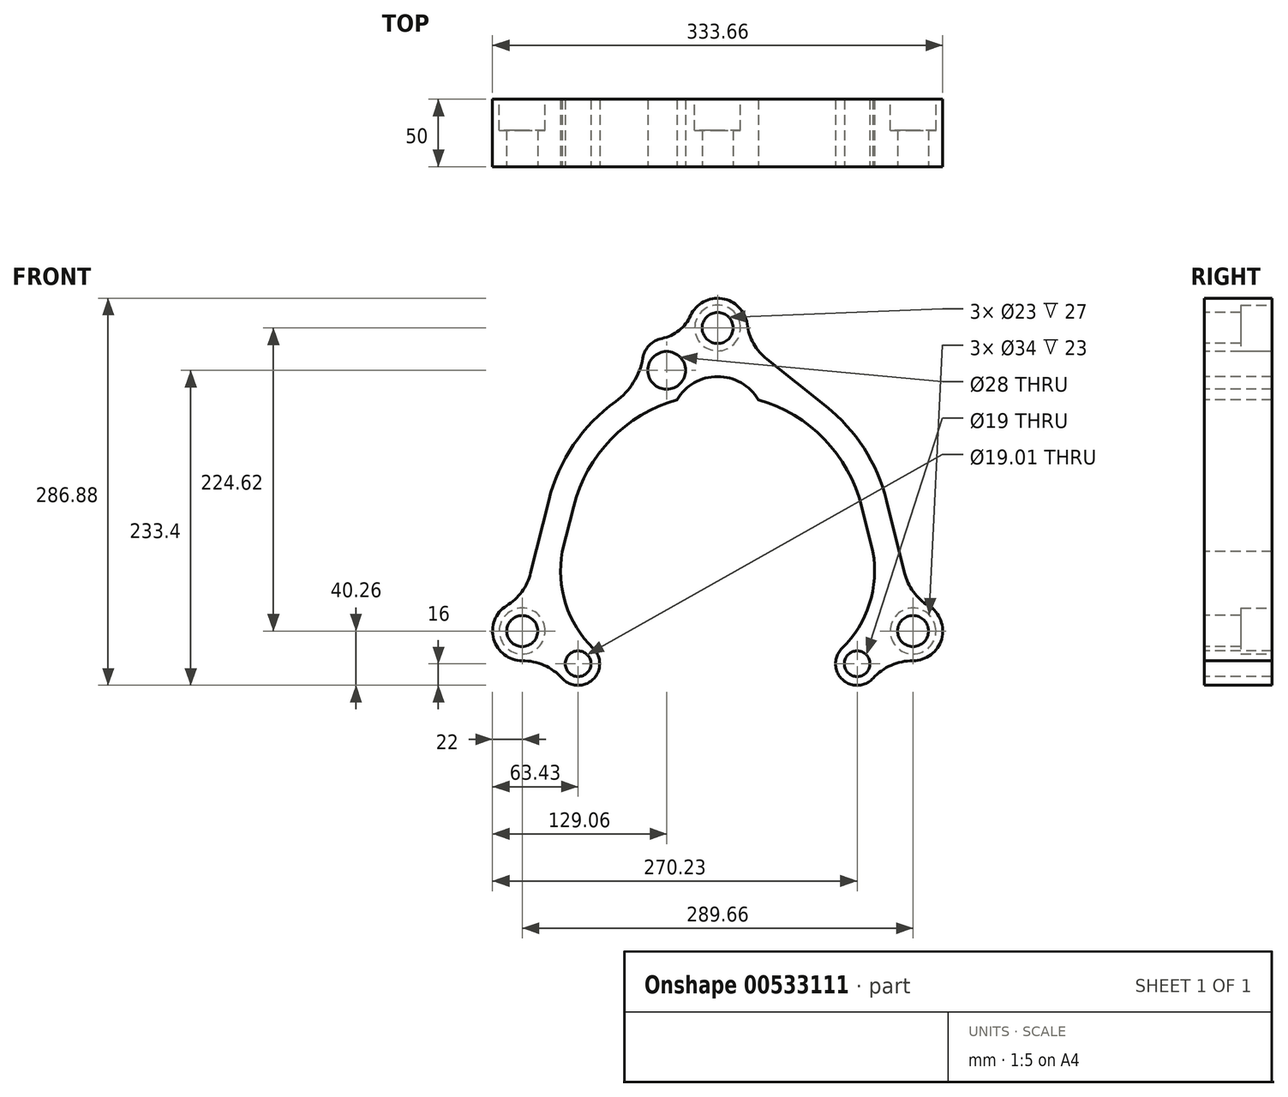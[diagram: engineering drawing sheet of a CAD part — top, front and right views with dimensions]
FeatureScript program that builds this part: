
annotation { "Feature Type Name" : "Feature", "Feature Type Description" : "" }
export const myFeature = defineFeature(function(context is Context, id is Id, definition is map)
    precondition{}
    {
        {
            var Q0;
            Q0=qCreatedBy(makeId("Front.planeOp"),FACE);
            var sketch = newSketch(context, id + "F0", { "sketchPlane" : qUnion([Q0])});
            skArc(sketch, "E0", {"start": v(-30.14, 105.79) * mm, "mid": v(-79.06, 76.48) * mm, "end": v(-106.73, 26.61) * mm});
            skArc(sketch, "E1", {"start": v(30.14, 105.79) * mm, "mid": v(0, 123) * mm, "end": v(-30.14, 105.79) * mm});
            skPoint(sketch, "E2.endSnap0", {"position": v(0, -110) * mm});
            skArc(sketch, "E3", {"start": v(144.8, -87.62) * mm, "mid": v(166, -71.63) * mm, "end": v(156.38, -46.9) * mm});
            skArc(sketch, "E4", {"start": v(125.17, 31.2) * mm, "mid": v(108.5, 69.79) * mm, "end": v(80.3, 100.96) * mm});
            skLineSegment(sketch, "E5", {"start": v(125.17, 31.2) * mm, "end": v(138.57, -22.53) * mm});
            skArc(sketch, "E6", {"start": v(138.57, -22.53) * mm, "mid": v(145.09, -36.46) * mm, "end": v(156.38, -46.9) * mm});
            skLineSegment(sketch, "E7", {"start": v(36.58, 135.74) * mm, "end": v(80.3, 100.96) * mm});
            skArc(sketch, "E8", {"start": v(21.81, 161.85) * mm, "mid": v(3.28, 180.75) * mm, "end": v(-20, 168.15) * mm});
            skArc(sketch, "E9", {"start": v(21.81, 161.85) * mm, "mid": v(26.65, 147.36) * mm, "end": v(36.58, 135.74) * mm});
            skArc(sketch, "E10", {"start": v(-41.34, 151.23) * mm, "mid": v(-50.68, 146.13) * mm, "end": v(-55.5, 136.64) * mm});
            skArc(sketch, "E11", {"start": v(-41.34, 151.23) * mm, "mid": v(-28.64, 157.13) * mm, "end": v(-20, 168.15) * mm});
            skArc(sketch, "E12", {"start": v(-75.52, 104.59) * mm, "mid": v(-62.37, 118.65) * mm, "end": v(-55.5, 136.64) * mm});
            skArc(sketch, "E13.trimOffspring", {"start": v(-75.52, 104.59) * mm, "mid": v(-106.84, 72.3) * mm, "end": v(-125.17, 31.2) * mm});
            skPoint(sketch, "E14.trimOffspring.center.orphan", {"position": v(5.86, 0) * mm});
            skArc(sketch, "E15.trimOffspring", {"start": v(106.73, 26.61) * mm, "mid": v(79.06, 76.48) * mm, "end": v(30.14, 105.79) * mm});
            skArc(sketch, "E16", {"start": v(92.23, -78.43) * mm, "mid": v(92.28, -101.38) * mm, "end": v(115.22, -100.66) * mm});
            skArc(sketch, "E17", {"start": v(144.8, -87.62) * mm, "mid": v(128.64, -91.02) * mm, "end": v(115.22, -100.66) * mm});
            skArc(sketch, "E18", {"start": v(92.23, -78.43) * mm, "mid": v(112.58, -45.47) * mm, "end": v(115.07, -6.82) * mm});
            skLineSegment(sketch, "E19", {"start": v(106.73, 26.61) * mm, "end": v(115.07, -6.82) * mm});
            skLineSegment(sketch, "E20", {"start": v(0, 88) * mm, "end": v(0, -110) * mm});
            skLineSegment(sketch, "E21.MirrorCS", {"start": v(-106.73, 26.61) * mm, "end": v(-115.07, -6.82) * mm});
            skLineSegment(sketch, "E22.MirrorCS", {"start": v(-125.17, 31.2) * mm, "end": v(-138.57, -22.53) * mm});
            skArc(sketch, "E23.MirrorCS", {"start": v(-138.57, -22.53) * mm, "mid": v(-145.09, -36.46) * mm, "end": v(-156.38, -46.9) * mm});
            skArc(sketch, "E24.MirrorCS", {"start": v(-144.8, -87.62) * mm, "mid": v(-166, -71.63) * mm, "end": v(-156.38, -46.9) * mm});
            skArc(sketch, "E25.MirrorCS", {"start": v(-144.8, -87.62) * mm, "mid": v(-128.64, -91.02) * mm, "end": v(-115.22, -100.66) * mm});
            skArc(sketch, "E26.MirrorCS", {"start": v(-92.23, -78.43) * mm, "mid": v(-92.28, -101.38) * mm, "end": v(-115.22, -100.66) * mm});
            skArc(sketch, "E27.MirrorCS", {"start": v(-92.23, -78.43) * mm, "mid": v(-112.58, -45.47) * mm, "end": v(-115.07, -6.82) * mm});
            skSolve(sketch);
        }
        {
            var Q0;
            Q0 = qSketchRegion(id + "F0", true);
            extrude(context, id + "F1", {"entities" : qUnion([Q0]), "oppositeDirection" : true, "depth" : 50 * mm, "offsetDistance" : 25 * mm});
        }
        {
            var Q0;
            Q0=qCreatedBy(makeId("Front.planeOp"),FACE);
            var sketch = newSketch(context, id + "F2", { "sketchPlane" : qUnion([Q0])});
            skCircle(sketch, "E28", {"center": v(0, 159) * mm, "radius": 11.5 * mm});
            skCircle(sketch, "E29", {"center": v(144.83, -65.62) * mm, "radius": 11.5 * mm});
            skCircle(sketch, "E30", {"center": v(-144.83, -65.62) * mm, "radius": 11.5 * mm});
            skSolve(sketch);
        }
        {
            var Q0;
            Q0 = qSketchRegion(id + "F2", true);
            extrude(context, id + "F3", {"entities" : qUnion([Q0]), "operationType" : NewBodyOperationType.REMOVE, "oppositeDirection" : true, "depth" : 64 * mm, "offsetDistance" : 25 * mm});
        }
        {
            var Q0;
            Q0=qCreatedBy(makeId("Front.planeOp"),FACE);
            var sketch = newSketch(context, id + "F4", { "sketchPlane" : qUnion([Q0])});
            skCircle(sketch, "E31", {"center": v(-37.77, 127.52) * mm, "radius": 14 * mm});
            skSolve(sketch);
        }
        {
            var Q0;
            Q0 = qSketchRegion(id + "F4", true);
            extrude(context, id + "F5", {"entities" : qUnion([Q0]), "operationType" : NewBodyOperationType.REMOVE, "oppositeDirection" : true, "depth" : 62 * mm, "offsetDistance" : 25 * mm});
        }
        {
            var Q0;
            Q0=qCreatedBy(makeId("Front.planeOp"),FACE);
            var sketch = newSketch(context, id + "F6", { "sketchPlane" : qUnion([Q0])});
            skCircle(sketch, "E32", {"center": v(-103.4, -89.88) * mm, "radius": 9.5 * mm});
            skCircle(sketch, "E33", {"center": v(103.4, -89.88) * mm, "radius": 9.5 * mm});
            skSolve(sketch);
        }
        {
            var Q0;
            Q0 = qSketchRegion(id + "F6", true);
            extrude(context, id + "F7", {"entities" : qUnion([Q0]), "operationType" : NewBodyOperationType.REMOVE, "oppositeDirection" : true, "depth" : 58 * mm, "offsetDistance" : 25 * mm});
        }
        {
            var Q0;
            Q0=makeQuery(id+"F1.opExtrude","CAP_FACE",FACE,{"disambiguationData":[OSD([sQuery(id+"F0.wireOp",EDGE,"E0"),sQuery(id+"F0.wireOp",EDGE,"E1"),sQuery(id+"F0.wireOp",EDGE,"E3"),sQuery(id+"F0.wireOp",EDGE,"E4"),sQuery(id+"F0.wireOp",EDGE,"E5"),sQuery(id+"F0.wireOp",EDGE,"E6"),sQuery(id+"F0.wireOp",EDGE,"E7"),sQuery(id+"F0.wireOp",EDGE,"E8"),sQuery(id+"F0.wireOp",EDGE,"E9"),sQuery(id+"F0.wireOp",EDGE,"E10"),sQuery(id+"F0.wireOp",EDGE,"E11"),sQuery(id+"F0.wireOp",EDGE,"E12"),sQuery(id+"F0.wireOp",EDGE,"E13.trimOffspring"),sQuery(id+"F0.wireOp",EDGE,"E15.trimOffspring"),sQuery(id+"F0.wireOp",EDGE,"E16"),sQuery(id+"F0.wireOp",EDGE,"E17"),sQuery(id+"F0.wireOp",EDGE,"E18"),sQuery(id+"F0.wireOp",EDGE,"E19"),sQuery(id+"F0.wireOp",EDGE,"E21.MirrorCS"),sQuery(id+"F0.wireOp",EDGE,"E22.MirrorCS"),sQuery(id+"F0.wireOp",EDGE,"E23.MirrorCS"),sQuery(id+"F0.wireOp",EDGE,"E24.MirrorCS"),sQuery(id+"F0.wireOp",EDGE,"E25.MirrorCS"),sQuery(id+"F0.wireOp",EDGE,"E26.MirrorCS"),sQuery(id+"F0.wireOp",EDGE,"E27.MirrorCS")])],"isStart":false});
            var sketch = newSketch(context, id + "F8", { "sketchPlane" : qUnion([Q0])});
            skCircle(sketch, "E34", {"center": v(-144.83, -65.62) * mm, "radius": 17 * mm});
            skCircle(sketch, "E35", {"center": v(144.83, -65.62) * mm, "radius": 17 * mm});
            skCircle(sketch, "E36", {"center": v(0, 159) * mm, "radius": 17 * mm});
            skSolve(sketch);
        }
        {
            var Q0;
            Q0 = qSketchRegion(id + "F8", true);
            extrude(context, id + "F9", {"entities" : qUnion([Q0]), "operationType" : NewBodyOperationType.REMOVE, "oppositeDirection" : true, "depth" : 23 * mm, "offsetDistance" : 25 * mm});
        }
    });
